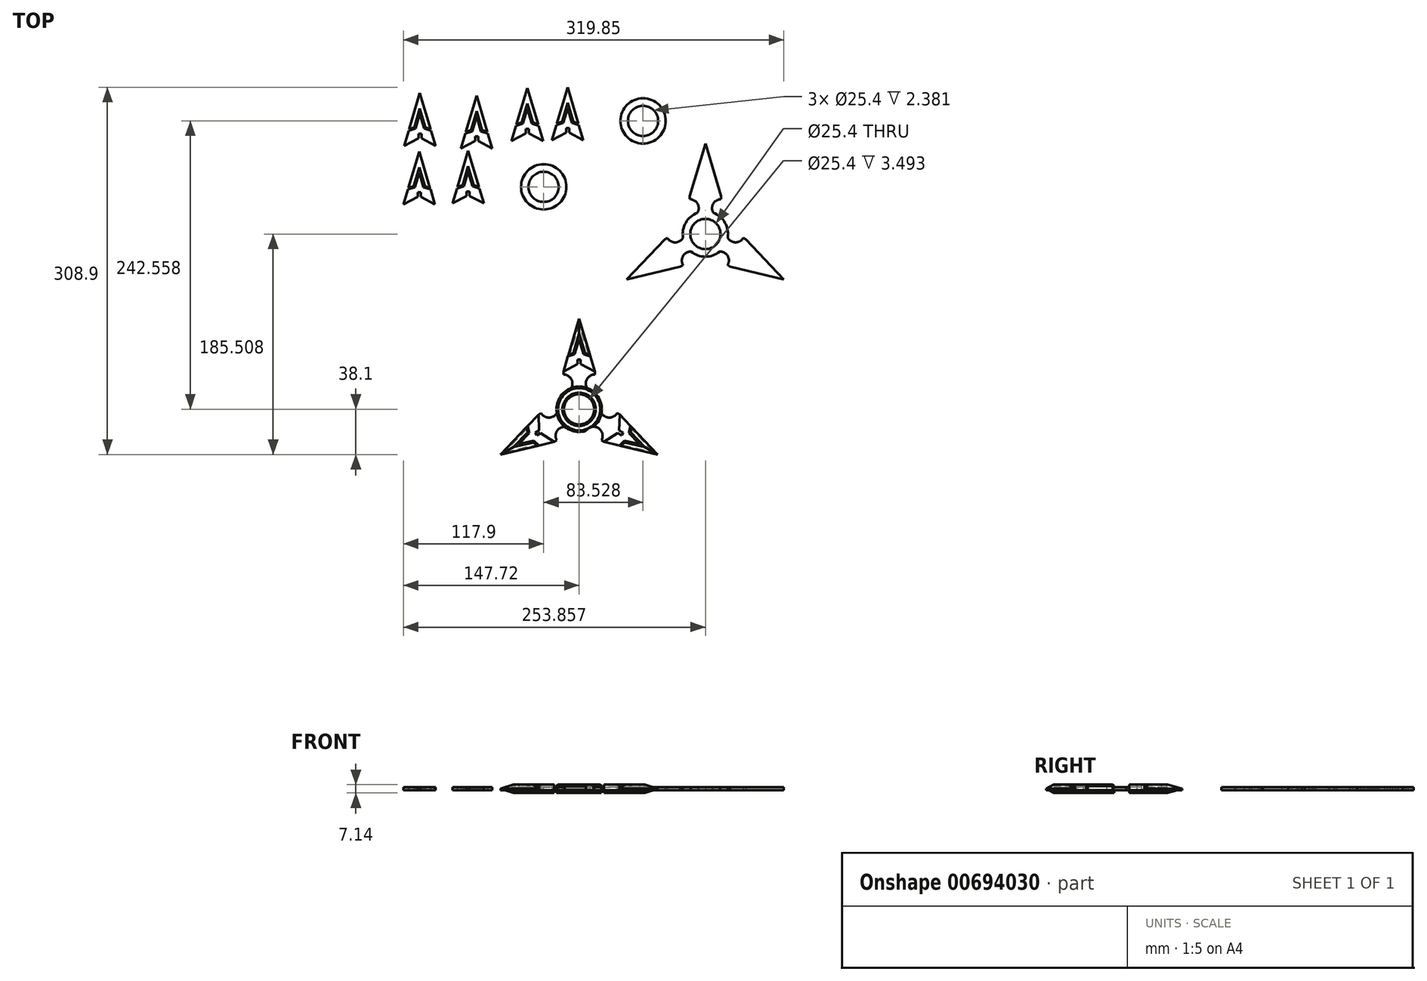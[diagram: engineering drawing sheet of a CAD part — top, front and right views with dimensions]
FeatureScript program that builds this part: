
annotation { "Feature Type Name" : "Feature", "Feature Type Description" : "" }
export const myFeature = defineFeature(function(context is Context, id is Id, definition is map)
    precondition{}
    {
        {
            var Q0;
            Q0=qCreatedBy(makeId("Top.planeOp"),FACE);
            var sketch = newSketch(context, id + "F0", { "sketchPlane" : qUnion([Q0])});
            skCircle(sketch, "E0", {"center": v(0, 0) * mm, "radius": 12.7 * mm});
            skCircle(sketch, "E1", {"center": v(0, 0) * mm, "radius": 19.05 * mm});
            skLineSegment(sketch, "E2", {"start": v(0, 76.2) * mm, "end": v(-13.25, 31.83) * mm});
            skLineSegment(sketch, "E3", {"start": v(13.25, 31.83) * mm, "end": v(0, 76.2) * mm});
            skLineSegment(sketch, "E4", {"start": v(-13.25, 31.83) * mm, "end": v(-13.25, 29.3) * mm});
            skLineSegment(sketch, "E5", {"start": v(13.25, 31.83) * mm, "end": v(13.25, 29.3) * mm});
            skLineSegment(sketch, "E6", {"start": v(0, 0) * mm, "end": v(-4, 18.62) * mm});
            skPoint(sketch, "E7", {"position": v(-12.85, 14.06) * mm});
            skPoint(sketch, "E8", {"position": v(12.85, 14.06) * mm});
            skArc(sketch, "E9", {"start": v(-12.85, 14.06) * mm, "mid": v(-5.63, 21.87) * mm, "end": v(-13.25, 29.3) * mm});
            skArc(sketch, "E10", {"start": v(13.25, 29.3) * mm, "mid": v(5.63, 21.87) * mm, "end": v(12.85, 14.06) * mm});
            skPoint(sketch, "E11", {"position": v(0, 63.05) * mm});
            skPoint(sketch, "E12", {"position": v(-4.73, 47.22) * mm});
            skPoint(sketch, "E13", {"position": v(4.73, 47.22) * mm});
            skPoint(sketch, "E14", {"position": v(-9.1, 45.72) * mm});
            skPoint(sketch, "E15", {"position": v(9.12, 45.67) * mm});
            skLineSegment(sketch, "E16", {"start": v(-9.1, 45.72) * mm, "end": v(-4.73, 47.22) * mm});
            skLineSegment(sketch, "E17", {"start": v(0, 63.05) * mm, "end": v(-4.73, 47.22) * mm});
            skLineSegment(sketch, "E18", {"start": v(0, 63.05) * mm, "end": v(4.73, 47.22) * mm});
            skLineSegment(sketch, "E19", {"start": v(4.73, 47.22) * mm, "end": v(9.12, 45.67) * mm});
            skPoint(sketch, "E20", {"position": v(-9.48, 44.45) * mm});
            skPoint(sketch, "E21", {"position": v(9.48, 44.45) * mm});
            skPoint(sketch, "E22", {"position": v(0, 58.62) * mm});
            skLineSegment(sketch, "E23", {"start": v(-13.25, 31.83) * mm, "end": v(-1.27, 38.1) * mm});
            skLineSegment(sketch, "E24", {"start": v(-1.27, 38.1) * mm, "end": v(-1.27, 41.91) * mm});
            skLineSegment(sketch, "E25", {"start": v(-1.27, 41.91) * mm, "end": v(1.27, 41.91) * mm});
            skLineSegment(sketch, "E26", {"start": v(1.27, 41.91) * mm, "end": v(1.27, 38.1) * mm});
            skLineSegment(sketch, "E27", {"start": v(1.27, 38.1) * mm, "end": v(13.25, 31.83) * mm});
            skLineSegment(sketch, "E28", {"start": v(-9.48, 44.45) * mm, "end": v(-3.7, 46.2) * mm});
            skLineSegment(sketch, "E29", {"start": v(-3.7, 46.2) * mm, "end": v(0, 58.62) * mm});
            skLineSegment(sketch, "E30", {"start": v(0, 58.62) * mm, "end": v(3.7, 46.2) * mm});
            skLineSegment(sketch, "E31", {"start": v(3.7, 46.2) * mm, "end": v(9.48, 44.45) * mm});
            skPoint(sketch, "E32.1.0", {"position": v(-43.23, -14.01) * mm});
            skLineSegment(sketch, "E32.1.1", {"start": v(-66, -38.1) * mm, "end": v(-20.94, -27.39) * mm});
            skLineSegment(sketch, "E32.1.2", {"start": v(-33.63, -17.95) * mm, "end": v(-34.2, -4.44) * mm});
            skPoint(sketch, "E32.1.3", {"position": v(-54.6, -31.53) * mm});
            skLineSegment(sketch, "E32.1.4", {"start": v(-20.94, -27.39) * mm, "end": v(-32.36, -20.15) * mm});
            skLineSegment(sketch, "E32.1.5", {"start": v(-34.2, -4.44) * mm, "end": v(-66, -38.1) * mm});
            skPoint(sketch, "E32.1.6", {"position": v(-33.75, -30.44) * mm});
            skLineSegment(sketch, "E32.1.7", {"start": v(-54.6, -31.53) * mm, "end": v(-38.52, -27.7) * mm});
            skPoint(sketch, "E32.1.8", {"position": v(-38.52, -27.7) * mm});
            skLineSegment(sketch, "E32.1.9", {"start": v(-50.76, -29.3) * mm, "end": v(-41.86, -19.89) * mm});
            skPoint(sketch, "E32.1.10", {"position": v(-44.1, -14.94) * mm});
            skLineSegment(sketch, "E32.1.11", {"start": v(-54.6, -31.53) * mm, "end": v(-43.25, -19.51) * mm});
            skPoint(sketch, "E32.1.12", {"position": v(-50.76, -29.3) * mm});
            skPoint(sketch, "E32.1.13", {"position": v(-43.25, -19.51) * mm});
            skPoint(sketch, "E32.1.14", {"position": v(-35.04, -30.74) * mm});
            skLineSegment(sketch, "E32.1.15", {"start": v(-38.15, -26.3) * mm, "end": v(-50.76, -29.3) * mm});
            skLineSegment(sketch, "E32.1.16", {"start": v(-41.86, -19.89) * mm, "end": v(-43.23, -14.01) * mm});
            skLineSegment(sketch, "E32.1.17", {"start": v(-36.93, -19.86) * mm, "end": v(-33.63, -17.95) * mm});
            skLineSegment(sketch, "E32.1.18", {"start": v(-43.25, -19.51) * mm, "end": v(-44.1, -14.94) * mm});
            skLineSegment(sketch, "E32.1.19", {"start": v(-33.75, -30.44) * mm, "end": v(-38.15, -26.3) * mm});
            skLineSegment(sketch, "E32.1.20", {"start": v(-35.04, -30.74) * mm, "end": v(-38.52, -27.7) * mm});
            skLineSegment(sketch, "E32.1.21", {"start": v(-35.66, -22.05) * mm, "end": v(-36.93, -19.86) * mm});
            skLineSegment(sketch, "E32.1.22", {"start": v(-32.36, -20.15) * mm, "end": v(-35.66, -22.05) * mm});
            skLineSegment(sketch, "E32.1.23", {"start": v(-34.2, -4.44) * mm, "end": v(-32, -3.17) * mm});
            skLineSegment(sketch, "E32.1.24", {"start": v(-20.94, -27.39) * mm, "end": v(-18.74, -26.12) * mm});
            skArc(sketch, "E32.1.25", {"start": v(-32, -3.17) * mm, "mid": v(-21.75, -6.06) * mm, "end": v(-18.6, 4.1) * mm});
            skArc(sketch, "E32.1.26", {"start": v(-5.75, -18.16) * mm, "mid": v(-16.12, -15.81) * mm, "end": v(-18.74, -26.12) * mm});
            skPoint(sketch, "E32.2.0", {"position": v(33.75, -30.44) * mm});
            skLineSegment(sketch, "E32.2.1", {"start": v(66, -38.1) * mm, "end": v(34.2, -4.44) * mm});
            skLineSegment(sketch, "E32.2.2", {"start": v(32.36, -20.15) * mm, "end": v(20.94, -27.39) * mm});
            skPoint(sketch, "E32.2.3", {"position": v(54.6, -31.53) * mm});
            skLineSegment(sketch, "E32.2.4", {"start": v(34.2, -4.44) * mm, "end": v(33.63, -17.95) * mm});
            skLineSegment(sketch, "E32.2.5", {"start": v(20.94, -27.39) * mm, "end": v(66, -38.1) * mm});
            skPoint(sketch, "E32.2.6", {"position": v(43.23, -14.01) * mm});
            skLineSegment(sketch, "E32.2.7", {"start": v(54.6, -31.53) * mm, "end": v(43.25, -19.51) * mm});
            skPoint(sketch, "E32.2.8", {"position": v(43.25, -19.51) * mm});
            skLineSegment(sketch, "E32.2.9", {"start": v(50.76, -29.3) * mm, "end": v(38.15, -26.3) * mm});
            skPoint(sketch, "E32.2.10", {"position": v(35, -30.73) * mm});
            skLineSegment(sketch, "E32.2.11", {"start": v(54.6, -31.53) * mm, "end": v(38.52, -27.7) * mm});
            skPoint(sketch, "E32.2.12", {"position": v(50.76, -29.3) * mm});
            skPoint(sketch, "E32.2.13", {"position": v(38.52, -27.7) * mm});
            skPoint(sketch, "E32.2.14", {"position": v(44.15, -14.98) * mm});
            skLineSegment(sketch, "E32.2.15", {"start": v(41.86, -19.89) * mm, "end": v(50.76, -29.3) * mm});
            skLineSegment(sketch, "E32.2.16", {"start": v(38.15, -26.3) * mm, "end": v(33.75, -30.44) * mm});
            skLineSegment(sketch, "E32.2.17", {"start": v(35.66, -22.05) * mm, "end": v(32.36, -20.15) * mm});
            skLineSegment(sketch, "E32.2.18", {"start": v(38.52, -27.7) * mm, "end": v(35, -30.73) * mm});
            skLineSegment(sketch, "E32.2.19", {"start": v(43.23, -14.01) * mm, "end": v(41.86, -19.89) * mm});
            skLineSegment(sketch, "E32.2.20", {"start": v(44.15, -14.98) * mm, "end": v(43.25, -19.51) * mm});
            skLineSegment(sketch, "E32.2.21", {"start": v(36.93, -19.86) * mm, "end": v(35.66, -22.05) * mm});
            skLineSegment(sketch, "E32.2.22", {"start": v(33.63, -17.95) * mm, "end": v(36.93, -19.86) * mm});
            skLineSegment(sketch, "E32.2.23", {"start": v(20.94, -27.39) * mm, "end": v(18.74, -26.12) * mm});
            skLineSegment(sketch, "E32.2.24", {"start": v(34.2, -4.44) * mm, "end": v(32, -3.17) * mm});
            skArc(sketch, "E32.2.25", {"start": v(18.74, -26.12) * mm, "mid": v(16.12, -15.81) * mm, "end": v(5.75, -18.16) * mm});
            skArc(sketch, "E32.2.26", {"start": v(18.6, 4.1) * mm, "mid": v(21.75, -6.06) * mm, "end": v(32, -3.17) * mm});
            skCircle(sketch, "E33", {"center": v(228.68, 14.43) * mm, "radius": 12.7 * mm});
            skCircle(sketch, "E34", {"center": v(228.68, 14.43) * mm, "radius": 19.05 * mm});
            skLineSegment(sketch, "E35", {"start": v(228.68, 90.63) * mm, "end": v(215.43, 46.27) * mm});
            skLineSegment(sketch, "E36", {"start": v(241.93, 46.27) * mm, "end": v(228.68, 90.63) * mm});
            skLineSegment(sketch, "E37", {"start": v(215.43, 46.27) * mm, "end": v(215.43, 43.73) * mm});
            skLineSegment(sketch, "E38", {"start": v(241.93, 46.27) * mm, "end": v(241.93, 43.73) * mm});
            skPoint(sketch, "E39", {"position": v(215.83, 28.5) * mm});
            skPoint(sketch, "E40", {"position": v(241.53, 28.5) * mm});
            skArc(sketch, "E41", {"start": v(215.83, 28.5) * mm, "mid": v(223.05, 36.3) * mm, "end": v(215.43, 43.73) * mm});
            skArc(sketch, "E42", {"start": v(241.93, 43.73) * mm, "mid": v(234.3, 36.3) * mm, "end": v(241.53, 28.5) * mm});
            skPoint(sketch, "E43", {"position": v(228.68, 77.49) * mm});
            skPoint(sketch, "E44", {"position": v(223.95, 61.65) * mm});
            skPoint(sketch, "E45", {"position": v(233.4, 61.65) * mm});
            skPoint(sketch, "E46", {"position": v(219.58, 60.15) * mm});
            skPoint(sketch, "E47", {"position": v(237.8, 60.1) * mm});
            skLineSegment(sketch, "E48", {"start": v(219.58, 60.15) * mm, "end": v(223.95, 61.65) * mm});
            skLineSegment(sketch, "E49", {"start": v(228.68, 77.49) * mm, "end": v(223.95, 61.65) * mm});
            skLineSegment(sketch, "E50", {"start": v(228.68, 77.49) * mm, "end": v(233.4, 61.65) * mm});
            skLineSegment(sketch, "E51", {"start": v(233.4, 61.65) * mm, "end": v(237.8, 60.1) * mm});
            skPoint(sketch, "E52", {"position": v(219.2, 58.88) * mm});
            skPoint(sketch, "E53", {"position": v(238.16, 58.88) * mm});
            skPoint(sketch, "E54", {"position": v(228.68, 73.05) * mm});
            skLineSegment(sketch, "E55", {"start": v(215.43, 46.27) * mm, "end": v(227.4, 52.53) * mm});
            skLineSegment(sketch, "E56", {"start": v(227.4, 52.53) * mm, "end": v(227.4, 56.34) * mm});
            skLineSegment(sketch, "E57", {"start": v(227.4, 56.34) * mm, "end": v(229.95, 56.34) * mm});
            skLineSegment(sketch, "E58", {"start": v(229.95, 56.34) * mm, "end": v(229.95, 52.53) * mm});
            skLineSegment(sketch, "E59", {"start": v(229.95, 52.53) * mm, "end": v(241.93, 46.27) * mm});
            skLineSegment(sketch, "E60", {"start": v(219.2, 58.88) * mm, "end": v(224.97, 60.63) * mm});
            skLineSegment(sketch, "E61", {"start": v(224.97, 60.63) * mm, "end": v(228.68, 73.05) * mm});
            skLineSegment(sketch, "E62", {"start": v(228.68, 73.05) * mm, "end": v(232.39, 60.63) * mm});
            skLineSegment(sketch, "E63", {"start": v(232.39, 60.63) * mm, "end": v(238.16, 58.88) * mm});
            skPoint(sketch, "E64.1.0", {"position": v(185.44, 0.42) * mm});
            skLineSegment(sketch, "E64.1.1", {"start": v(162.69, -23.67) * mm, "end": v(207.73, -12.95) * mm});
            skLineSegment(sketch, "E64.1.2", {"start": v(195.05, -3.52) * mm, "end": v(194.49, 10) * mm});
            skPoint(sketch, "E64.1.3", {"position": v(174.07, -17.1) * mm});
            skLineSegment(sketch, "E64.1.4", {"start": v(207.73, -12.95) * mm, "end": v(196.32, -5.72) * mm});
            skLineSegment(sketch, "E64.1.5", {"start": v(194.49, 10) * mm, "end": v(162.69, -23.67) * mm});
            skPoint(sketch, "E64.1.6", {"position": v(194.92, -16) * mm});
            skLineSegment(sketch, "E64.1.7", {"start": v(174.07, -17.1) * mm, "end": v(190.15, -13.27) * mm});
            skPoint(sketch, "E64.1.8", {"position": v(190.15, -13.27) * mm});
            skLineSegment(sketch, "E64.1.9", {"start": v(177.92, -14.87) * mm, "end": v(186.82, -5.45) * mm});
            skPoint(sketch, "E64.1.10", {"position": v(184.57, -0.5) * mm});
            skLineSegment(sketch, "E64.1.11", {"start": v(174.07, -17.1) * mm, "end": v(185.42, -5.08) * mm});
            skPoint(sketch, "E64.1.12", {"position": v(177.92, -14.87) * mm});
            skPoint(sketch, "E64.1.13", {"position": v(185.42, -5.08) * mm});
            skPoint(sketch, "E64.1.14", {"position": v(193.63, -16.3) * mm});
            skLineSegment(sketch, "E64.1.15", {"start": v(190.52, -11.88) * mm, "end": v(177.92, -14.87) * mm});
            skLineSegment(sketch, "E64.1.16", {"start": v(186.82, -5.45) * mm, "end": v(185.44, 0.42) * mm});
            skLineSegment(sketch, "E64.1.17", {"start": v(191.75, -5.42) * mm, "end": v(195.05, -3.52) * mm});
            skLineSegment(sketch, "E64.1.18", {"start": v(185.42, -5.08) * mm, "end": v(184.57, -0.5) * mm});
            skLineSegment(sketch, "E64.1.19", {"start": v(194.92, -16) * mm, "end": v(190.52, -11.88) * mm});
            skLineSegment(sketch, "E64.1.20", {"start": v(193.63, -16.3) * mm, "end": v(190.15, -13.27) * mm});
            skLineSegment(sketch, "E64.1.21", {"start": v(193.02, -7.62) * mm, "end": v(191.75, -5.42) * mm});
            skLineSegment(sketch, "E64.1.22", {"start": v(196.32, -5.72) * mm, "end": v(193.02, -7.62) * mm});
            skLineSegment(sketch, "E64.1.23", {"start": v(194.49, 10) * mm, "end": v(196.69, 11.26) * mm});
            skLineSegment(sketch, "E64.1.24", {"start": v(207.73, -12.95) * mm, "end": v(209.93, -11.68) * mm});
            skArc(sketch, "E64.1.25", {"start": v(196.69, 11.26) * mm, "mid": v(206.92, 8.38) * mm, "end": v(210.07, 18.53) * mm});
            skArc(sketch, "E64.1.26", {"start": v(222.93, -3.73) * mm, "mid": v(212.55, -1.38) * mm, "end": v(209.93, -11.68) * mm});
            skPoint(sketch, "E64.2.0", {"position": v(262.43, -16) * mm});
            skLineSegment(sketch, "E64.2.1", {"start": v(294.67, -23.67) * mm, "end": v(262.87, 10) * mm});
            skLineSegment(sketch, "E64.2.2", {"start": v(261.04, -5.72) * mm, "end": v(249.62, -12.95) * mm});
            skPoint(sketch, "E64.2.3", {"position": v(283.28, -17.1) * mm});
            skLineSegment(sketch, "E64.2.4", {"start": v(262.87, 10) * mm, "end": v(262.3, -3.52) * mm});
            skLineSegment(sketch, "E64.2.5", {"start": v(249.62, -12.95) * mm, "end": v(294.67, -23.67) * mm});
            skPoint(sketch, "E64.2.6", {"position": v(271.91, 0.42) * mm});
            skLineSegment(sketch, "E64.2.7", {"start": v(283.28, -17.1) * mm, "end": v(271.93, -5.08) * mm});
            skPoint(sketch, "E64.2.8", {"position": v(271.93, -5.08) * mm});
            skLineSegment(sketch, "E64.2.9", {"start": v(279.44, -14.87) * mm, "end": v(266.83, -11.88) * mm});
            skPoint(sketch, "E64.2.10", {"position": v(263.67, -16.3) * mm});
            skLineSegment(sketch, "E64.2.11", {"start": v(283.28, -17.1) * mm, "end": v(267.2, -13.27) * mm});
            skPoint(sketch, "E64.2.12", {"position": v(279.44, -14.87) * mm});
            skPoint(sketch, "E64.2.13", {"position": v(267.2, -13.27) * mm});
            skPoint(sketch, "E64.2.14", {"position": v(272.82, -0.54) * mm});
            skLineSegment(sketch, "E64.2.15", {"start": v(270.54, -5.45) * mm, "end": v(279.44, -14.87) * mm});
            skLineSegment(sketch, "E64.2.16", {"start": v(266.83, -11.88) * mm, "end": v(262.43, -16) * mm});
            skLineSegment(sketch, "E64.2.17", {"start": v(264.34, -7.62) * mm, "end": v(261.04, -5.72) * mm});
            skLineSegment(sketch, "E64.2.18", {"start": v(267.2, -13.27) * mm, "end": v(263.67, -16.3) * mm});
            skLineSegment(sketch, "E64.2.19", {"start": v(271.91, 0.42) * mm, "end": v(270.54, -5.45) * mm});
            skLineSegment(sketch, "E64.2.20", {"start": v(272.82, -0.54) * mm, "end": v(271.93, -5.08) * mm});
            skLineSegment(sketch, "E64.2.21", {"start": v(265.6, -5.42) * mm, "end": v(264.34, -7.62) * mm});
            skLineSegment(sketch, "E64.2.22", {"start": v(262.3, -3.52) * mm, "end": v(265.6, -5.42) * mm});
            skLineSegment(sketch, "E64.2.23", {"start": v(249.62, -12.95) * mm, "end": v(247.42, -11.68) * mm});
            skLineSegment(sketch, "E64.2.24", {"start": v(262.87, 10) * mm, "end": v(260.67, 11.26) * mm});
            skArc(sketch, "E64.2.25", {"start": v(247.42, -11.68) * mm, "mid": v(244.8, -1.38) * mm, "end": v(234.43, -3.73) * mm});
            skArc(sketch, "E64.2.26", {"start": v(247.28, 18.53) * mm, "mid": v(250.43, 8.38) * mm, "end": v(260.67, 11.26) * mm});
            skSolve(sketch);
        }
        {
            var Q0;
            Q0=makeQuery(id+"F0.imprint","IMPRINT",FACE,{"disambiguationData":[TD([[makeQuery(id+"F0.imprint","IMPRINT",EDGE,{"derivedFrom":sQuery(id+"F0.wireOp",EDGE,"E32.2.2")}),-1.0]])]});
            var Q1;
            Q1=makeQuery(id+"F0.imprint","IMPRINT",FACE,{"disambiguationData":[TD([[makeQuery(id+"F0.imprint","IMPRINT",EDGE,{"derivedFrom":sQuery(id+"F0.wireOp",EDGE,"E32.1.2")}),-1.0]])]});
            var Q2;
            {var subQ5=sQuery(id+"F0.wireOp",EDGE,"E4");Q2=makeQuery(id+"F0.imprint","IMPRINT",FACE,{"disambiguationData":[TD([[makeQuery(id+"F0.imprint","IMPRINT",EDGE,{"derivedFrom":subQ5}),1.0]])]});}
            var Q3;
            {var subQ1=sQuery(id+"F0.wireOp",EDGE,"E16");Q3=makeQuery(id+"F0.imprint","IMPRINT",FACE,{"disambiguationData":[TD([[makeQuery(id+"F0.imprint","IMPRINT",EDGE,{"derivedFrom":subQ1}),-1.0]])]});}
            var Q4;
            Q4=makeQuery(id+"F0.imprint","IMPRINT",FACE,{"disambiguationData":[TD([[makeQuery(id+"F0.imprint","IMPRINT",EDGE,{"derivedFrom":sQuery(id+"F0.wireOp",EDGE,"E32.2.7")}),1.0]])]});
            var Q5;
            Q5=makeQuery(id+"F0.imprint","IMPRINT",FACE,{"disambiguationData":[TD([[makeQuery(id+"F0.imprint","IMPRINT",EDGE,{"derivedFrom":sQuery(id+"F0.wireOp",EDGE,"E32.1.7")}),1.0]])]});
            extrude(context, id + "F1", {"entities" : qUnion([Q0, Q1, Q2, Q3, Q4, Q5]), "depth" : 2.38 * mm, "offsetDistance" : 25.4 * mm});
        }
        {
            var Q0;
            {var subQ2=sQuery(id+"F0.wireOp",EDGE,"E23");Q0=makeQuery(id+"F0.imprint","IMPRINT",FACE,{"disambiguationData":[TD([[makeQuery(id+"F0.imprint","IMPRINT",EDGE,{"derivedFrom":subQ2}),1.0]])]});}
            var Q1;
            {var subQ0=sQuery(id+"F0.wireOp",EDGE,"E16");Q1=makeQuery(id+"F0.imprint","IMPRINT",FACE,{"disambiguationData":[TD([[makeQuery(id+"F0.imprint","IMPRINT",EDGE,{"derivedFrom":subQ0}),1.0]])]});}
            var Q2;
            {var subQ4=sQuery(id+"F0.wireOp",EDGE,"E32.2.2");Q2=makeQuery(id+"F0.imprint","IMPRINT",FACE,{"disambiguationData":[TD([[makeQuery(id+"F0.imprint","IMPRINT",EDGE,{"derivedFrom":subQ4}),1.0]])]});}
            var Q3;
            Q3=makeQuery(id+"F0.imprint","IMPRINT",FACE,{"disambiguationData":[TD([[makeQuery(id+"F0.imprint","IMPRINT",EDGE,{"derivedFrom":sQuery(id+"F0.wireOp",EDGE,"E32.2.7")}),-1.0]])]});
            var Q4;
            Q4=makeQuery(id+"F0.imprint","IMPRINT",FACE,{"disambiguationData":[TD([[makeQuery(id+"F0.imprint","IMPRINT",EDGE,{"derivedFrom":sQuery(id+"F0.wireOp",EDGE,"E32.1.7")}),-1.0]])]});
            var Q5;
            {var subQ4=sQuery(id+"F0.wireOp",EDGE,"E32.1.2");Q5=makeQuery(id+"F0.imprint","IMPRINT",FACE,{"disambiguationData":[TD([[makeQuery(id+"F0.imprint","IMPRINT",EDGE,{"derivedFrom":subQ4}),1.0]])]});}
            var Q6;
            Q6=makeQuery(id+"F0.imprint","IMPRINT",FACE,{"disambiguationData":[TD([[makeQuery(id+"F0.imprint","IMPRINT",EDGE,{"derivedFrom":sQuery(id+"F0.wireOp",EDGE,"E0")}),-1.0]])]});
            var Q7;
            {var subQ0=sQuery(id+"F0.wireOp",EDGE,"E32.2.26");var subQ1=sQuery(id+"F0.wireOp",EDGE,"E1");var subQ2=makeQuery(id+"F0.imprint","INTERSECT",VERTEX,{"disambiguationData":[OD(0.0)],"derivedFrom":[subQ1,subQ0]});Q7=makeQuery(id+"F0.imprint","IMPRINT",FACE,{"disambiguationData":[TD([[makeQuery(id+"F0.imprint","IMPRINT",EDGE,{"disambiguationData":[TD([[subQ2,1.0]])],"derivedFrom":subQ1}),1.0]])]});}
            var Q8;
            {var subQ0=sQuery(id+"F0.wireOp",EDGE,"E32.2.25");var subQ1=sQuery(id+"F0.wireOp",EDGE,"E1");var subQ2=makeQuery(id+"F0.imprint","INTERSECT",VERTEX,{"disambiguationData":[OD(0.0)],"derivedFrom":[subQ1,subQ0]});Q8=makeQuery(id+"F0.imprint","IMPRINT",FACE,{"disambiguationData":[TD([[makeQuery(id+"F0.imprint","IMPRINT",EDGE,{"disambiguationData":[TD([[subQ2,-1.0]])],"derivedFrom":subQ1}),1.0]])]});}
            var Q9;
            {var subQ0=sQuery(id+"F0.wireOp",EDGE,"E32.1.26");var subQ1=sQuery(id+"F0.wireOp",EDGE,"E1");var subQ2=makeQuery(id+"F0.imprint","INTERSECT",VERTEX,{"disambiguationData":[OD(0.0)],"derivedFrom":[subQ1,subQ0]});Q9=makeQuery(id+"F0.imprint","IMPRINT",FACE,{"disambiguationData":[TD([[makeQuery(id+"F0.imprint","IMPRINT",EDGE,{"disambiguationData":[TD([[subQ2,1.0]])],"derivedFrom":subQ1}),1.0]])]});}
            var Q10;
            {var subQ0=sQuery(id+"F0.wireOp",EDGE,"E32.1.25");var subQ1=sQuery(id+"F0.wireOp",EDGE,"E1");var subQ2=makeQuery(id+"F0.imprint","INTERSECT",VERTEX,{"disambiguationData":[OD(0.0)],"derivedFrom":[subQ1,subQ0]});Q10=makeQuery(id+"F0.imprint","IMPRINT",FACE,{"disambiguationData":[TD([[makeQuery(id+"F0.imprint","IMPRINT",EDGE,{"disambiguationData":[TD([[subQ2,-1.0]])],"derivedFrom":subQ1}),1.0]])]});}
            var Q11;
            {var subQ0=sQuery(id+"F0.wireOp",EDGE,"E9");var subQ1=sQuery(id+"F0.wireOp",EDGE,"E1");var subQ2=makeQuery(id+"F0.imprint","INTERSECT",VERTEX,{"disambiguationData":[OD(0.0)],"derivedFrom":[subQ1,subQ0]});Q11=makeQuery(id+"F0.imprint","IMPRINT",FACE,{"disambiguationData":[TD([[makeQuery(id+"F0.imprint","IMPRINT",EDGE,{"disambiguationData":[TD([[subQ2,1.0]])],"derivedFrom":subQ1}),1.0]])]});}
            var Q12;
            {var subQ0=sQuery(id+"F0.wireOp",EDGE,"E10");var subQ1=sQuery(id+"F0.wireOp",EDGE,"E1");var subQ2=makeQuery(id+"F0.imprint","INTERSECT",VERTEX,{"disambiguationData":[OD(0.0)],"derivedFrom":[subQ1,subQ0]});Q12=makeQuery(id+"F0.imprint","IMPRINT",FACE,{"disambiguationData":[TD([[makeQuery(id+"F0.imprint","IMPRINT",EDGE,{"disambiguationData":[TD([[subQ2,-1.0]])],"derivedFrom":subQ1}),1.0]])]});}
            extrude(context, id + "F2", {"entities" : qUnion([Q0, Q1, Q2, Q3, Q4, Q5, Q6, Q7, Q8, Q9, Q10, Q11, Q12]), "depth" : 4.76 * mm, "offsetDistance" : 25.4 * mm});
        }
        {
            var Q0;
            Q0=makeQuery(id+"F0.imprint","IMPRINT",FACE,{"disambiguationData":[TD([[makeQuery(id+"F0.imprint","IMPRINT",EDGE,{"derivedFrom":sQuery(id+"F0.wireOp",EDGE,"E0")}),-1.0]])]});
            var Q1;
            {var subQ0=sQuery(id+"F0.wireOp",EDGE,"E32.2.25");var subQ1=sQuery(id+"F0.wireOp",EDGE,"E1");var subQ2=makeQuery(id+"F0.imprint","INTERSECT",VERTEX,{"disambiguationData":[OD(0.0)],"derivedFrom":[subQ1,subQ0]});Q1=makeQuery(id+"F0.imprint","IMPRINT",FACE,{"disambiguationData":[TD([[makeQuery(id+"F0.imprint","IMPRINT",EDGE,{"disambiguationData":[TD([[subQ2,-1.0]])],"derivedFrom":subQ1}),1.0]])]});}
            var Q2;
            {var subQ0=sQuery(id+"F0.wireOp",EDGE,"E32.1.26");var subQ1=sQuery(id+"F0.wireOp",EDGE,"E1");var subQ2=makeQuery(id+"F0.imprint","INTERSECT",VERTEX,{"disambiguationData":[OD(0.0)],"derivedFrom":[subQ1,subQ0]});Q2=makeQuery(id+"F0.imprint","IMPRINT",FACE,{"disambiguationData":[TD([[makeQuery(id+"F0.imprint","IMPRINT",EDGE,{"disambiguationData":[TD([[subQ2,1.0]])],"derivedFrom":subQ1}),1.0]])]});}
            var Q3;
            {var subQ0=sQuery(id+"F0.wireOp",EDGE,"E32.1.25");var subQ1=sQuery(id+"F0.wireOp",EDGE,"E1");var subQ2=makeQuery(id+"F0.imprint","INTERSECT",VERTEX,{"disambiguationData":[OD(0.0)],"derivedFrom":[subQ1,subQ0]});Q3=makeQuery(id+"F0.imprint","IMPRINT",FACE,{"disambiguationData":[TD([[makeQuery(id+"F0.imprint","IMPRINT",EDGE,{"disambiguationData":[TD([[subQ2,-1.0]])],"derivedFrom":subQ1}),1.0]])]});}
            var Q4;
            {var subQ0=sQuery(id+"F0.wireOp",EDGE,"E9");var subQ1=sQuery(id+"F0.wireOp",EDGE,"E1");var subQ2=makeQuery(id+"F0.imprint","INTERSECT",VERTEX,{"disambiguationData":[OD(0.0)],"derivedFrom":[subQ1,subQ0]});Q4=makeQuery(id+"F0.imprint","IMPRINT",FACE,{"disambiguationData":[TD([[makeQuery(id+"F0.imprint","IMPRINT",EDGE,{"disambiguationData":[TD([[subQ2,1.0]])],"derivedFrom":subQ1}),1.0]])]});}
            var Q5;
            {var subQ0=sQuery(id+"F0.wireOp",EDGE,"E10");var subQ1=sQuery(id+"F0.wireOp",EDGE,"E1");var subQ2=makeQuery(id+"F0.imprint","INTERSECT",VERTEX,{"disambiguationData":[OD(0.0)],"derivedFrom":[subQ1,subQ0]});Q5=makeQuery(id+"F0.imprint","IMPRINT",FACE,{"disambiguationData":[TD([[makeQuery(id+"F0.imprint","IMPRINT",EDGE,{"disambiguationData":[TD([[subQ2,-1.0]])],"derivedFrom":subQ1}),1.0]])]});}
            var Q6;
            {var subQ4=sQuery(id+"F0.wireOp",EDGE,"E32.2.2");Q6=makeQuery(id+"F0.imprint","IMPRINT",FACE,{"disambiguationData":[TD([[makeQuery(id+"F0.imprint","IMPRINT",EDGE,{"derivedFrom":subQ4}),1.0]])]});}
            var Q7;
            Q7=makeQuery(id+"F0.imprint","IMPRINT",FACE,{"disambiguationData":[TD([[makeQuery(id+"F0.imprint","IMPRINT",EDGE,{"derivedFrom":sQuery(id+"F0.wireOp",EDGE,"E32.2.7")}),-1.0]])]});
            var Q8;
            {var subQ4=sQuery(id+"F0.wireOp",EDGE,"E32.1.2");Q8=makeQuery(id+"F0.imprint","IMPRINT",FACE,{"disambiguationData":[TD([[makeQuery(id+"F0.imprint","IMPRINT",EDGE,{"derivedFrom":subQ4}),1.0]])]});}
            var Q9;
            Q9=makeQuery(id+"F0.imprint","IMPRINT",FACE,{"disambiguationData":[TD([[makeQuery(id+"F0.imprint","IMPRINT",EDGE,{"derivedFrom":sQuery(id+"F0.wireOp",EDGE,"E32.1.7")}),-1.0]])]});
            var Q10;
            {var subQ2=sQuery(id+"F0.wireOp",EDGE,"E23");Q10=makeQuery(id+"F0.imprint","IMPRINT",FACE,{"disambiguationData":[TD([[makeQuery(id+"F0.imprint","IMPRINT",EDGE,{"derivedFrom":subQ2}),1.0]])]});}
            var Q11;
            {var subQ0=sQuery(id+"F0.wireOp",EDGE,"E16");Q11=makeQuery(id+"F0.imprint","IMPRINT",FACE,{"disambiguationData":[TD([[makeQuery(id+"F0.imprint","IMPRINT",EDGE,{"derivedFrom":subQ0}),1.0]])]});}
            extrude(context, id + "F3", {"entities" : qUnion([Q0, Q1, Q2, Q3, Q4, Q5, Q6, Q7, Q8, Q9, Q10, Q11]), "oppositeDirection" : true, "depth" : 2.38 * mm, "offsetDistance" : 25.4 * mm});
        }
        {
            var Q0;
            {var subQ0=sQuery(id+"F0.wireOp",EDGE,"E32.1.1");Q0=makeQuery(id+"F2.opExtrude","CAP_EDGE",EDGE,{"disambiguationData":[OSD([subQ0]),TDD([makeQuery(id+"F0.imprint","IMPRINT",EDGE,{"disambiguationData":[TD([[makeQuery(id+"F0.imprint","INTERSECT",VERTEX,{"derivedFrom":[subQ0,sQuery(id+"F0.wireOp",EDGE,"E32.1.5")]}),-1.0]])],"derivedFrom":subQ0})])],"isStart":false});}
            var Q1;
            {var subQ0=sQuery(id+"F0.wireOp",EDGE,"E32.1.1");Q1=makeQuery(id+"F3.opExtrude","CAP_EDGE",EDGE,{"disambiguationData":[OSD([subQ0]),TDD([makeQuery(id+"F0.imprint","IMPRINT",EDGE,{"disambiguationData":[TD([[makeQuery(id+"F0.imprint","INTERSECT",VERTEX,{"derivedFrom":[subQ0,sQuery(id+"F0.wireOp",EDGE,"E32.1.5")]}),-1.0]])],"derivedFrom":subQ0})])],"isStart":false});}
            var Q2;
            {var subQ0=sQuery(id+"F0.wireOp",EDGE,"E32.1.5");Q2=makeQuery(id+"F2.opExtrude","CAP_EDGE",EDGE,{"disambiguationData":[OSD([subQ0]),TDD([makeQuery(id+"F0.imprint","IMPRINT",EDGE,{"disambiguationData":[TD([[makeQuery(id+"F0.imprint","INTERSECT",VERTEX,{"derivedFrom":[sQuery(id+"F0.wireOp",EDGE,"E32.1.1"),subQ0]}),1.0]])],"derivedFrom":subQ0})])],"isStart":false});}
            var Q3;
            {var subQ0=sQuery(id+"F0.wireOp",EDGE,"E32.1.5");Q3=makeQuery(id+"F3.opExtrude","CAP_EDGE",EDGE,{"disambiguationData":[OSD([subQ0]),TDD([makeQuery(id+"F0.imprint","IMPRINT",EDGE,{"disambiguationData":[TD([[makeQuery(id+"F0.imprint","INTERSECT",VERTEX,{"derivedFrom":[sQuery(id+"F0.wireOp",EDGE,"E32.1.1"),subQ0]}),1.0]])],"derivedFrom":subQ0})])],"isStart":false});}
            var Q4;
            {var subQ0=sQuery(id+"F0.wireOp",EDGE,"E32.2.5");Q4=makeQuery(id+"F2.opExtrude","CAP_EDGE",EDGE,{"disambiguationData":[OSD([subQ0]),TDD([makeQuery(id+"F0.imprint","IMPRINT",EDGE,{"disambiguationData":[TD([[makeQuery(id+"F0.imprint","INTERSECT",VERTEX,{"derivedFrom":[sQuery(id+"F0.wireOp",EDGE,"E32.2.1"),subQ0]}),1.0]])],"derivedFrom":subQ0})])],"isStart":false});}
            var Q5;
            {var subQ0=sQuery(id+"F0.wireOp",EDGE,"E32.2.5");Q5=makeQuery(id+"F3.opExtrude","CAP_EDGE",EDGE,{"disambiguationData":[OSD([subQ0]),TDD([makeQuery(id+"F0.imprint","IMPRINT",EDGE,{"disambiguationData":[TD([[makeQuery(id+"F0.imprint","INTERSECT",VERTEX,{"derivedFrom":[sQuery(id+"F0.wireOp",EDGE,"E32.2.1"),subQ0]}),1.0]])],"derivedFrom":subQ0})])],"isStart":false});}
            var Q6;
            {var subQ0=sQuery(id+"F0.wireOp",EDGE,"E32.2.1");Q6=makeQuery(id+"F2.opExtrude","CAP_EDGE",EDGE,{"disambiguationData":[OSD([subQ0]),TDD([makeQuery(id+"F0.imprint","IMPRINT",EDGE,{"disambiguationData":[TD([[makeQuery(id+"F0.imprint","INTERSECT",VERTEX,{"derivedFrom":[subQ0,sQuery(id+"F0.wireOp",EDGE,"E32.2.5")]}),-1.0]])],"derivedFrom":subQ0})])],"isStart":false});}
            var Q7;
            {var subQ0=sQuery(id+"F0.wireOp",EDGE,"E32.2.1");Q7=makeQuery(id+"F3.opExtrude","CAP_EDGE",EDGE,{"disambiguationData":[OSD([subQ0]),TDD([makeQuery(id+"F0.imprint","IMPRINT",EDGE,{"disambiguationData":[TD([[makeQuery(id+"F0.imprint","INTERSECT",VERTEX,{"derivedFrom":[subQ0,sQuery(id+"F0.wireOp",EDGE,"E32.2.5")]}),-1.0]])],"derivedFrom":subQ0})])],"isStart":false});}
            var Q8;
            {var subQ0=sQuery(id+"F0.wireOp",EDGE,"E3");Q8=makeQuery(id+"F2.opExtrude","CAP_EDGE",EDGE,{"disambiguationData":[OSD([subQ0]),TDD([makeQuery(id+"F0.imprint","IMPRINT",EDGE,{"disambiguationData":[TD([[makeQuery(id+"F0.imprint","INTERSECT",VERTEX,{"derivedFrom":[sQuery(id+"F0.wireOp",EDGE,"E2"),subQ0]}),1.0]])],"derivedFrom":subQ0})])],"isStart":false});}
            var Q9;
            {var subQ0=sQuery(id+"F0.wireOp",EDGE,"E3");Q9=makeQuery(id+"F3.opExtrude","CAP_EDGE",EDGE,{"disambiguationData":[OSD([subQ0]),TDD([makeQuery(id+"F0.imprint","IMPRINT",EDGE,{"disambiguationData":[TD([[makeQuery(id+"F0.imprint","INTERSECT",VERTEX,{"derivedFrom":[sQuery(id+"F0.wireOp",EDGE,"E2"),subQ0]}),1.0]])],"derivedFrom":subQ0})])],"isStart":false});}
            var Q10;
            {var subQ0=sQuery(id+"F0.wireOp",EDGE,"E2");Q10=makeQuery(id+"F3.opExtrude","CAP_EDGE",EDGE,{"disambiguationData":[OSD([subQ0]),TDD([makeQuery(id+"F0.imprint","IMPRINT",EDGE,{"disambiguationData":[TD([[makeQuery(id+"F0.imprint","INTERSECT",VERTEX,{"derivedFrom":[subQ0,sQuery(id+"F0.wireOp",EDGE,"E3")]}),-1.0]])],"derivedFrom":subQ0})])],"isStart":false});}
            var Q11;
            {var subQ0=sQuery(id+"F0.wireOp",EDGE,"E2");Q11=makeQuery(id+"F2.opExtrude","CAP_EDGE",EDGE,{"disambiguationData":[OSD([subQ0]),TDD([makeQuery(id+"F0.imprint","IMPRINT",EDGE,{"disambiguationData":[TD([[makeQuery(id+"F0.imprint","INTERSECT",VERTEX,{"derivedFrom":[subQ0,sQuery(id+"F0.wireOp",EDGE,"E3")]}),-1.0]])],"derivedFrom":subQ0})])],"isStart":false});}
            chamfer(context, id + "F4", {"entities" : qUnion([Q0, Q1, Q2, Q3, Q4, Q5, Q6, Q7, Q8, Q9, Q10, Q11]), "width" : 3.57 * mm, "tangentPropagation" : true});
        }
        {
            var Q0;
            Q0=makeQuery(id+"F2.opExtrude","CAP_EDGE",EDGE,{"disambiguationData":[OSD([sQuery(id+"F0.wireOp",EDGE,"E1")])],"isStart":false});
            var Q1;
            Q1=makeQuery(id+"F2.opExtrude","CAP_EDGE",EDGE,{"disambiguationData":[OSD([sQuery(id+"F0.wireOp",EDGE,"E0")])],"isStart":false});
            chamfer(context, id + "F5", {"entities" : qUnion([Q0, Q1]), "width" : 1.27 * mm, "tangentPropagation" : true});
        }
        {
            var Q0;
            Q0=qCreatedBy(makeId("Top.planeOp"),FACE);
            var sketch = newSketch(context, id + "F6", { "sketchPlane" : qUnion([Q0])});
            skCircle(sketch, "E65", {"center": v(106.14, 147.4) * mm, "radius": 12.7 * mm});
            skCircle(sketch, "E66", {"center": v(106.14, 147.4) * mm, "radius": 19.05 * mm});
            skLineSegment(sketch, "E67", {"start": v(106.14, 223.6) * mm, "end": v(92.89, 179.24) * mm});
            skLineSegment(sketch, "E68", {"start": v(119.39, 179.24) * mm, "end": v(106.14, 223.6) * mm});
            skLineSegment(sketch, "E69", {"start": v(92.89, 179.24) * mm, "end": v(92.89, 176.7) * mm});
            skLineSegment(sketch, "E70", {"start": v(119.39, 179.24) * mm, "end": v(119.39, 176.7) * mm});
            skLineSegment(sketch, "E71.1.1", {"start": v(40.08, 109.3) * mm, "end": v(85.13, 120.02) * mm});
            skLineSegment(sketch, "E71.1.5", {"start": v(71.88, 142.97) * mm, "end": v(40.08, 109.3) * mm});
            skLineSegment(sketch, "E71.1.23", {"start": v(71.88, 142.97) * mm, "end": v(74.08, 144.24) * mm});
            skLineSegment(sketch, "E71.1.24", {"start": v(85.13, 120.02) * mm, "end": v(87.38, 121.32) * mm});
            skLineSegment(sketch, "E71.2.1", {"start": v(172.13, 109.3) * mm, "end": v(140.33, 142.97) * mm});
            skLineSegment(sketch, "E71.2.5", {"start": v(127.08, 120.02) * mm, "end": v(172.13, 109.3) * mm});
            skLineSegment(sketch, "E71.2.23", {"start": v(127.08, 120.02) * mm, "end": v(124.88, 121.29) * mm});
            skLineSegment(sketch, "E71.2.24", {"start": v(140.33, 142.97) * mm, "end": v(138.13, 144.24) * mm});
            skPoint(sketch, "E72", {"position": v(118.27, 132.72) * mm});
            skPoint(sketch, "E73", {"position": v(94, 132.72) * mm});
            skPoint(sketch, "E74", {"position": v(99.48, 165.26) * mm});
            skPoint(sketch, "E75", {"position": v(112.8, 165.26) * mm});
            skPoint(sketch, "E76", {"position": v(124.92, 144.25) * mm});
            skArc(sketch, "E77", {"start": v(74.08, 144.24) * mm, "mid": v(80.72, 140.37) * mm, "end": v(87.35, 144.25) * mm});
            skArc(sketch, "E78", {"start": v(94, 132.72) * mm, "mid": v(87.4, 128.93) * mm, "end": v(87.38, 121.32) * mm});
            skArc(sketch, "E79", {"start": v(124.92, 144.25) * mm, "mid": v(131.52, 140.42) * mm, "end": v(138.13, 144.24) * mm});
            skArc(sketch, "E80", {"start": v(124.88, 121.29) * mm, "mid": v(124.88, 128.91) * mm, "end": v(118.27, 132.72) * mm});
            skArc(sketch, "E81", {"start": v(119.39, 176.7) * mm, "mid": v(112.78, 172.88) * mm, "end": v(112.8, 165.26) * mm});
            skArc(sketch, "E82", {"start": v(99.48, 165.26) * mm, "mid": v(99.5, 172.89) * mm, "end": v(92.89, 176.7) * mm});
            skSolve(sketch);
        }
        {
            var Q0;
            Q0=makeQuery(id+"F6.imprint","IMPRINT",FACE,{"disambiguationData":[TD([[makeQuery(id+"F6.imprint","IMPRINT",EDGE,{"derivedFrom":sQuery(id+"F6.wireOp",EDGE,"E71.2.1")}),1.0]])]});
            var Q1;
            Q1=makeQuery(id+"F6.imprint","IMPRINT",FACE,{"disambiguationData":[TD([[makeQuery(id+"F6.imprint","IMPRINT",EDGE,{"derivedFrom":sQuery(id+"F6.wireOp",EDGE,"E71.1.1")}),1.0]])]});
            var Q2;
            Q2=makeQuery(id+"F6.imprint","IMPRINT",FACE,{"disambiguationData":[TD([[makeQuery(id+"F6.imprint","IMPRINT",EDGE,{"derivedFrom":sQuery(id+"F6.wireOp",EDGE,"E67")}),1.0]])]});
            var Q3;
            Q3=makeQuery(id+"F6.imprint","IMPRINT",FACE,{"disambiguationData":[TD([[makeQuery(id+"F6.imprint","IMPRINT",EDGE,{"derivedFrom":sQuery(id+"F6.wireOp",EDGE,"E65")}),-1.0]])]});
            extrude(context, id + "F7", {"entities" : qUnion([Q0, Q1, Q2, Q3]), "depth" : 2.38 * mm, "offsetDistance" : 25.4 * mm});
        }
        {
            var Q0;
            Q0=qCreatedBy(makeId("Top.planeOp"),FACE);
            var sketch = newSketch(context, id + "F8", { "sketchPlane" : qUnion([Q0])});
            skPoint(sketch, "E83", {"position": v(-86.25, 250.64) * mm});
            skPoint(sketch, "E84", {"position": v(-90.98, 234.8) * mm});
            skPoint(sketch, "E85", {"position": v(-81.52, 234.8) * mm});
            skPoint(sketch, "E86", {"position": v(-95.35, 233.3) * mm});
            skPoint(sketch, "E87", {"position": v(-77.13, 233.25) * mm});
            skLineSegment(sketch, "E88", {"start": v(-95.35, 233.3) * mm, "end": v(-90.98, 234.8) * mm});
            skLineSegment(sketch, "E89", {"start": v(-86.25, 250.64) * mm, "end": v(-90.98, 234.8) * mm});
            skLineSegment(sketch, "E90", {"start": v(-86.25, 250.64) * mm, "end": v(-81.52, 234.8) * mm});
            skLineSegment(sketch, "E91", {"start": v(-81.52, 234.8) * mm, "end": v(-77.13, 233.25) * mm});
            skPoint(sketch, "E92", {"position": v(-95.73, 232.04) * mm});
            skPoint(sketch, "E93", {"position": v(-76.77, 232.04) * mm});
            skPoint(sketch, "E94", {"position": v(-86.25, 246.2) * mm});
            skLineSegment(sketch, "E95", {"start": v(-99.5, 219.42) * mm, "end": v(-87.52, 225.69) * mm});
            skLineSegment(sketch, "E96", {"start": v(-87.52, 225.69) * mm, "end": v(-87.52, 229.5) * mm});
            skLineSegment(sketch, "E97", {"start": v(-87.52, 229.5) * mm, "end": v(-84.98, 229.5) * mm});
            skLineSegment(sketch, "E98", {"start": v(-84.98, 229.5) * mm, "end": v(-84.98, 225.69) * mm});
            skLineSegment(sketch, "E99", {"start": v(-84.98, 225.69) * mm, "end": v(-73, 219.42) * mm});
            skLineSegment(sketch, "E100", {"start": v(-95.73, 232.04) * mm, "end": v(-89.96, 233.78) * mm});
            skLineSegment(sketch, "E101", {"start": v(-89.96, 233.78) * mm, "end": v(-86.25, 246.2) * mm});
            skLineSegment(sketch, "E102", {"start": v(-86.25, 246.2) * mm, "end": v(-82.54, 233.78) * mm});
            skLineSegment(sketch, "E103", {"start": v(-82.54, 233.78) * mm, "end": v(-76.77, 232.04) * mm});
            skLineSegment(sketch, "E104", {"start": v(-95.35, 233.3) * mm, "end": v(-86.25, 263.79) * mm});
            skLineSegment(sketch, "E105", {"start": v(-77.13, 233.25) * mm, "end": v(-86.25, 263.79) * mm});
            skLineSegment(sketch, "E106", {"start": v(-76.77, 232.04) * mm, "end": v(-73, 219.42) * mm});
            skLineSegment(sketch, "E107", {"start": v(-95.73, 232.04) * mm, "end": v(-99.5, 219.42) * mm});
            skPoint(sketch, "E108", {"position": v(-43.55, 257.07) * mm});
            skPoint(sketch, "E109", {"position": v(-48.28, 241.23) * mm});
            skPoint(sketch, "E110", {"position": v(-38.83, 241.23) * mm});
            skPoint(sketch, "E111", {"position": v(-52.66, 239.73) * mm});
            skPoint(sketch, "E112", {"position": v(-34.44, 239.68) * mm});
            skLineSegment(sketch, "E113", {"start": v(-52.66, 239.73) * mm, "end": v(-48.28, 241.23) * mm});
            skLineSegment(sketch, "E114", {"start": v(-43.55, 257.07) * mm, "end": v(-48.28, 241.23) * mm});
            skLineSegment(sketch, "E115", {"start": v(-43.55, 257.07) * mm, "end": v(-38.83, 241.23) * mm});
            skLineSegment(sketch, "E116", {"start": v(-38.83, 241.23) * mm, "end": v(-34.44, 239.68) * mm});
            skPoint(sketch, "E117", {"position": v(-53.03, 238.46) * mm});
            skPoint(sketch, "E118", {"position": v(-34.07, 238.46) * mm});
            skPoint(sketch, "E119", {"position": v(-43.55, 252.63) * mm});
            skLineSegment(sketch, "E120", {"start": v(-56.8, 225.84) * mm, "end": v(-44.82, 232.11) * mm});
            skLineSegment(sketch, "E121", {"start": v(-44.82, 232.11) * mm, "end": v(-44.82, 235.92) * mm});
            skLineSegment(sketch, "E122", {"start": v(-44.82, 235.92) * mm, "end": v(-42.28, 235.92) * mm});
            skLineSegment(sketch, "E123", {"start": v(-42.28, 235.92) * mm, "end": v(-42.28, 232.11) * mm});
            skLineSegment(sketch, "E124", {"start": v(-42.28, 232.11) * mm, "end": v(-30.3, 225.84) * mm});
            skLineSegment(sketch, "E125", {"start": v(-53.03, 238.46) * mm, "end": v(-47.26, 240.21) * mm});
            skLineSegment(sketch, "E126", {"start": v(-47.26, 240.21) * mm, "end": v(-43.55, 252.63) * mm});
            skLineSegment(sketch, "E127", {"start": v(-43.55, 252.63) * mm, "end": v(-39.85, 240.21) * mm});
            skLineSegment(sketch, "E128", {"start": v(-39.85, 240.21) * mm, "end": v(-34.07, 238.46) * mm});
            skLineSegment(sketch, "E129", {"start": v(-52.66, 239.73) * mm, "end": v(-43.55, 270.21) * mm});
            skLineSegment(sketch, "E130", {"start": v(-34.44, 239.68) * mm, "end": v(-43.55, 270.21) * mm});
            skLineSegment(sketch, "E131", {"start": v(-34.07, 238.46) * mm, "end": v(-30.3, 225.84) * mm});
            skLineSegment(sketch, "E132", {"start": v(-53.03, 238.46) * mm, "end": v(-56.8, 225.84) * mm});
            skPoint(sketch, "E133", {"position": v(-9.72, 257.66) * mm});
            skPoint(sketch, "E134", {"position": v(-14.45, 241.82) * mm});
            skPoint(sketch, "E135", {"position": v(-4.99, 241.82) * mm});
            skPoint(sketch, "E136", {"position": v(-18.82, 240.32) * mm});
            skPoint(sketch, "E137", {"position": v(-0.6, 240.27) * mm});
            skLineSegment(sketch, "E138", {"start": v(-18.82, 240.32) * mm, "end": v(-14.45, 241.82) * mm});
            skLineSegment(sketch, "E139", {"start": v(-9.72, 257.66) * mm, "end": v(-14.45, 241.82) * mm});
            skLineSegment(sketch, "E140", {"start": v(-9.72, 257.66) * mm, "end": v(-4.99, 241.82) * mm});
            skLineSegment(sketch, "E141", {"start": v(-4.99, 241.82) * mm, "end": v(-0.6, 240.27) * mm});
            skPoint(sketch, "E142", {"position": v(-19.2, 239.05) * mm});
            skPoint(sketch, "E143", {"position": v(-0.24, 239.05) * mm});
            skPoint(sketch, "E144", {"position": v(-9.72, 253.22) * mm});
            skLineSegment(sketch, "E145", {"start": v(-22.97, 226.43) * mm, "end": v(-10.99, 232.7) * mm});
            skLineSegment(sketch, "E146", {"start": v(-10.99, 232.7) * mm, "end": v(-10.99, 236.51) * mm});
            skLineSegment(sketch, "E147", {"start": v(-10.99, 236.51) * mm, "end": v(-8.45, 236.51) * mm});
            skLineSegment(sketch, "E148", {"start": v(-8.45, 236.51) * mm, "end": v(-8.45, 232.7) * mm});
            skLineSegment(sketch, "E149", {"start": v(-8.45, 232.7) * mm, "end": v(3.53, 226.43) * mm});
            skLineSegment(sketch, "E150", {"start": v(-19.2, 239.05) * mm, "end": v(-13.43, 240.8) * mm});
            skLineSegment(sketch, "E151", {"start": v(-13.43, 240.8) * mm, "end": v(-9.72, 253.22) * mm});
            skLineSegment(sketch, "E152", {"start": v(-9.72, 253.22) * mm, "end": v(-6, 240.8) * mm});
            skLineSegment(sketch, "E153", {"start": v(-6, 240.8) * mm, "end": v(-0.24, 239.05) * mm});
            skLineSegment(sketch, "E154", {"start": v(-18.82, 240.32) * mm, "end": v(-9.72, 270.8) * mm});
            skLineSegment(sketch, "E155", {"start": v(-0.6, 240.27) * mm, "end": v(-9.72, 270.8) * mm});
            skLineSegment(sketch, "E156", {"start": v(-0.24, 239.05) * mm, "end": v(3.53, 226.43) * mm});
            skLineSegment(sketch, "E157", {"start": v(-19.2, 239.05) * mm, "end": v(-22.97, 226.43) * mm});
            skPoint(sketch, "E158", {"position": v(-133.88, 252.95) * mm});
            skPoint(sketch, "E159", {"position": v(-138.61, 237.1) * mm});
            skPoint(sketch, "E160", {"position": v(-129.16, 237.1) * mm});
            skPoint(sketch, "E161", {"position": v(-142.99, 235.61) * mm});
            skPoint(sketch, "E162", {"position": v(-124.77, 235.56) * mm});
            skLineSegment(sketch, "E163", {"start": v(-142.99, 235.61) * mm, "end": v(-138.61, 237.1) * mm});
            skLineSegment(sketch, "E164", {"start": v(-133.88, 252.95) * mm, "end": v(-138.61, 237.1) * mm});
            skLineSegment(sketch, "E165", {"start": v(-133.88, 252.95) * mm, "end": v(-129.16, 237.1) * mm});
            skLineSegment(sketch, "E166", {"start": v(-129.16, 237.1) * mm, "end": v(-124.77, 235.56) * mm});
            skPoint(sketch, "E167", {"position": v(-143.36, 234.34) * mm});
            skPoint(sketch, "E168", {"position": v(-124.4, 234.34) * mm});
            skPoint(sketch, "E169", {"position": v(-133.88, 248.5) * mm});
            skLineSegment(sketch, "E170", {"start": v(-147.13, 221.73) * mm, "end": v(-135.15, 228) * mm});
            skLineSegment(sketch, "E171", {"start": v(-135.15, 228) * mm, "end": v(-135.15, 231.8) * mm});
            skLineSegment(sketch, "E172", {"start": v(-135.15, 231.8) * mm, "end": v(-132.61, 231.8) * mm});
            skLineSegment(sketch, "E173", {"start": v(-132.61, 231.8) * mm, "end": v(-132.61, 228) * mm});
            skLineSegment(sketch, "E174", {"start": v(-132.61, 228) * mm, "end": v(-120.64, 221.73) * mm});
            skLineSegment(sketch, "E175", {"start": v(-143.36, 234.34) * mm, "end": v(-137.6, 236.1) * mm});
            skLineSegment(sketch, "E176", {"start": v(-137.6, 236.1) * mm, "end": v(-133.88, 248.5) * mm});
            skLineSegment(sketch, "E177", {"start": v(-133.88, 248.5) * mm, "end": v(-130.18, 236.1) * mm});
            skLineSegment(sketch, "E178", {"start": v(-130.18, 236.1) * mm, "end": v(-124.4, 234.34) * mm});
            skLineSegment(sketch, "E179", {"start": v(-142.99, 235.61) * mm, "end": v(-133.88, 266.1) * mm});
            skLineSegment(sketch, "E180", {"start": v(-124.77, 235.56) * mm, "end": v(-133.88, 266.1) * mm});
            skLineSegment(sketch, "E181", {"start": v(-124.4, 234.34) * mm, "end": v(-120.64, 221.73) * mm});
            skLineSegment(sketch, "E182", {"start": v(-143.36, 234.34) * mm, "end": v(-147.13, 221.73) * mm});
            skPoint(sketch, "E183", {"position": v(-134.47, 203.52) * mm});
            skPoint(sketch, "E184", {"position": v(-139.2, 187.68) * mm});
            skPoint(sketch, "E185", {"position": v(-129.74, 187.68) * mm});
            skPoint(sketch, "E186", {"position": v(-143.57, 186.18) * mm});
            skPoint(sketch, "E187", {"position": v(-125.36, 186.13) * mm});
            skLineSegment(sketch, "E188", {"start": v(-143.57, 186.18) * mm, "end": v(-139.2, 187.68) * mm});
            skLineSegment(sketch, "E189", {"start": v(-134.47, 203.52) * mm, "end": v(-139.2, 187.68) * mm});
            skLineSegment(sketch, "E190", {"start": v(-134.47, 203.52) * mm, "end": v(-129.74, 187.68) * mm});
            skLineSegment(sketch, "E191", {"start": v(-129.74, 187.68) * mm, "end": v(-125.36, 186.13) * mm});
            skPoint(sketch, "E192", {"position": v(-143.95, 184.91) * mm});
            skPoint(sketch, "E193", {"position": v(-125, 184.91) * mm});
            skPoint(sketch, "E194", {"position": v(-134.47, 199.08) * mm});
            skLineSegment(sketch, "E195", {"start": v(-147.72, 172.3) * mm, "end": v(-135.74, 178.56) * mm});
            skLineSegment(sketch, "E196", {"start": v(-135.74, 178.56) * mm, "end": v(-135.74, 182.37) * mm});
            skLineSegment(sketch, "E197", {"start": v(-135.74, 182.37) * mm, "end": v(-133.2, 182.37) * mm});
            skLineSegment(sketch, "E198", {"start": v(-133.2, 182.37) * mm, "end": v(-133.2, 178.56) * mm});
            skLineSegment(sketch, "E199", {"start": v(-133.2, 178.56) * mm, "end": v(-121.23, 172.3) * mm});
            skLineSegment(sketch, "E200", {"start": v(-143.95, 184.91) * mm, "end": v(-138.18, 186.66) * mm});
            skLineSegment(sketch, "E201", {"start": v(-138.18, 186.66) * mm, "end": v(-134.47, 199.08) * mm});
            skLineSegment(sketch, "E202", {"start": v(-134.47, 199.08) * mm, "end": v(-130.77, 186.66) * mm});
            skLineSegment(sketch, "E203", {"start": v(-130.77, 186.66) * mm, "end": v(-125, 184.91) * mm});
            skLineSegment(sketch, "E204", {"start": v(-143.57, 186.18) * mm, "end": v(-134.47, 216.66) * mm});
            skLineSegment(sketch, "E205", {"start": v(-125.36, 186.13) * mm, "end": v(-134.47, 216.66) * mm});
            skLineSegment(sketch, "E206", {"start": v(-125, 184.91) * mm, "end": v(-121.23, 172.3) * mm});
            skLineSegment(sketch, "E207", {"start": v(-143.95, 184.91) * mm, "end": v(-147.72, 172.3) * mm});
            skPoint(sketch, "E208", {"position": v(-93.28, 204.4) * mm});
            skPoint(sketch, "E209", {"position": v(-98, 188.56) * mm});
            skPoint(sketch, "E210", {"position": v(-88.55, 188.56) * mm});
            skPoint(sketch, "E211", {"position": v(-102.38, 187.07) * mm});
            skPoint(sketch, "E212", {"position": v(-84.16, 187.01) * mm});
            skLineSegment(sketch, "E213", {"start": v(-102.38, 187.07) * mm, "end": v(-98, 188.56) * mm});
            skLineSegment(sketch, "E214", {"start": v(-93.28, 204.4) * mm, "end": v(-98, 188.56) * mm});
            skLineSegment(sketch, "E215", {"start": v(-93.28, 204.4) * mm, "end": v(-88.55, 188.56) * mm});
            skLineSegment(sketch, "E216", {"start": v(-88.55, 188.56) * mm, "end": v(-84.16, 187.01) * mm});
            skPoint(sketch, "E217", {"position": v(-102.76, 185.8) * mm});
            skPoint(sketch, "E218", {"position": v(-83.8, 185.8) * mm});
            skPoint(sketch, "E219", {"position": v(-93.28, 199.96) * mm});
            skLineSegment(sketch, "E220", {"start": v(-106.53, 173.18) * mm, "end": v(-94.55, 179.45) * mm});
            skLineSegment(sketch, "E221", {"start": v(-94.55, 179.45) * mm, "end": v(-94.55, 183.26) * mm});
            skLineSegment(sketch, "E222", {"start": v(-94.55, 183.26) * mm, "end": v(-92.01, 183.26) * mm});
            skLineSegment(sketch, "E223", {"start": v(-92.01, 183.26) * mm, "end": v(-92.01, 179.45) * mm});
            skLineSegment(sketch, "E224", {"start": v(-92.01, 179.45) * mm, "end": v(-80.03, 173.18) * mm});
            skLineSegment(sketch, "E225", {"start": v(-102.76, 185.8) * mm, "end": v(-96.99, 187.54) * mm});
            skLineSegment(sketch, "E226", {"start": v(-96.99, 187.54) * mm, "end": v(-93.28, 199.96) * mm});
            skLineSegment(sketch, "E227", {"start": v(-93.28, 199.96) * mm, "end": v(-89.57, 187.54) * mm});
            skLineSegment(sketch, "E228", {"start": v(-89.57, 187.54) * mm, "end": v(-83.8, 185.8) * mm});
            skLineSegment(sketch, "E229", {"start": v(-102.38, 187.07) * mm, "end": v(-93.28, 217.55) * mm});
            skLineSegment(sketch, "E230", {"start": v(-84.16, 187.01) * mm, "end": v(-93.28, 217.55) * mm});
            skLineSegment(sketch, "E231", {"start": v(-83.8, 185.8) * mm, "end": v(-80.03, 173.18) * mm});
            skLineSegment(sketch, "E232", {"start": v(-102.76, 185.8) * mm, "end": v(-106.53, 173.18) * mm});
            skCircle(sketch, "E233", {"center": v(-29.82, 187.06) * mm, "radius": 12.7 * mm});
            skCircle(sketch, "E234", {"center": v(-29.82, 187.06) * mm, "radius": 19.05 * mm});
            skCircle(sketch, "E235", {"center": v(53.7, 242.56) * mm, "radius": 12.7 * mm});
            skCircle(sketch, "E236", {"center": v(53.7, 242.56) * mm, "radius": 19.05 * mm});
            skSolve(sketch);
        }
        {
            var Q0;
            Q0=makeQuery(id+"F8.imprint","IMPRINT",FACE,{"disambiguationData":[TD([[makeQuery(id+"F8.imprint","IMPRINT",EDGE,{"derivedFrom":sQuery(id+"F8.wireOp",EDGE,"E213")}),1.0]])]});
            var Q1;
            Q1=makeQuery(id+"F8.imprint","IMPRINT",FACE,{"disambiguationData":[TD([[makeQuery(id+"F8.imprint","IMPRINT",EDGE,{"derivedFrom":sQuery(id+"F8.wireOp",EDGE,"E220")}),1.0]])]});
            var Q2;
            Q2=makeQuery(id+"F8.imprint","IMPRINT",FACE,{"disambiguationData":[TD([[makeQuery(id+"F8.imprint","IMPRINT",EDGE,{"derivedFrom":sQuery(id+"F8.wireOp",EDGE,"E195")}),1.0]])]});
            var Q3;
            Q3=makeQuery(id+"F8.imprint","IMPRINT",FACE,{"disambiguationData":[TD([[makeQuery(id+"F8.imprint","IMPRINT",EDGE,{"derivedFrom":sQuery(id+"F8.wireOp",EDGE,"E188")}),1.0]])]});
            var Q4;
            Q4=makeQuery(id+"F8.imprint","IMPRINT",FACE,{"disambiguationData":[TD([[makeQuery(id+"F8.imprint","IMPRINT",EDGE,{"derivedFrom":sQuery(id+"F8.wireOp",EDGE,"E170")}),1.0]])]});
            var Q5;
            Q5=makeQuery(id+"F8.imprint","IMPRINT",FACE,{"disambiguationData":[TD([[makeQuery(id+"F8.imprint","IMPRINT",EDGE,{"derivedFrom":sQuery(id+"F8.wireOp",EDGE,"E163")}),1.0]])]});
            var Q6;
            Q6=makeQuery(id+"F8.imprint","IMPRINT",FACE,{"disambiguationData":[TD([[makeQuery(id+"F8.imprint","IMPRINT",EDGE,{"derivedFrom":sQuery(id+"F8.wireOp",EDGE,"E88")}),1.0]])]});
            var Q7;
            Q7=makeQuery(id+"F8.imprint","IMPRINT",FACE,{"disambiguationData":[TD([[makeQuery(id+"F8.imprint","IMPRINT",EDGE,{"derivedFrom":sQuery(id+"F8.wireOp",EDGE,"E95")}),1.0]])]});
            var Q8;
            Q8=makeQuery(id+"F8.imprint","IMPRINT",FACE,{"disambiguationData":[TD([[makeQuery(id+"F8.imprint","IMPRINT",EDGE,{"derivedFrom":sQuery(id+"F8.wireOp",EDGE,"E113")}),1.0]])]});
            var Q9;
            Q9=makeQuery(id+"F8.imprint","IMPRINT",FACE,{"disambiguationData":[TD([[makeQuery(id+"F8.imprint","IMPRINT",EDGE,{"derivedFrom":sQuery(id+"F8.wireOp",EDGE,"E120")}),1.0]])]});
            var Q10;
            Q10=makeQuery(id+"F8.imprint","IMPRINT",FACE,{"disambiguationData":[TD([[makeQuery(id+"F8.imprint","IMPRINT",EDGE,{"derivedFrom":sQuery(id+"F8.wireOp",EDGE,"E138")}),1.0]])]});
            var Q11;
            Q11=makeQuery(id+"F8.imprint","IMPRINT",FACE,{"disambiguationData":[TD([[makeQuery(id+"F8.imprint","IMPRINT",EDGE,{"derivedFrom":sQuery(id+"F8.wireOp",EDGE,"E145")}),1.0]])]});
            var Q12;
            Q12=makeQuery(id+"F8.imprint","IMPRINT",FACE,{"disambiguationData":[TD([[makeQuery(id+"F8.imprint","IMPRINT",EDGE,{"derivedFrom":sQuery(id+"F8.wireOp",EDGE,"E233")}),-1.0]])]});
            var Q13;
            Q13=makeQuery(id+"F8.imprint","IMPRINT",FACE,{"disambiguationData":[TD([[makeQuery(id+"F8.imprint","IMPRINT",EDGE,{"derivedFrom":sQuery(id+"F8.wireOp",EDGE,"E235")}),-1.0]])]});
            extrude(context, id + "F9", {"entities" : qUnion([Q0, Q1, Q2, Q3, Q4, Q5, Q6, Q7, Q8, Q9, Q10, Q11, Q12, Q13]), "depth" : 2.38 * mm, "offsetDistance" : 25.4 * mm});
        }
    });
